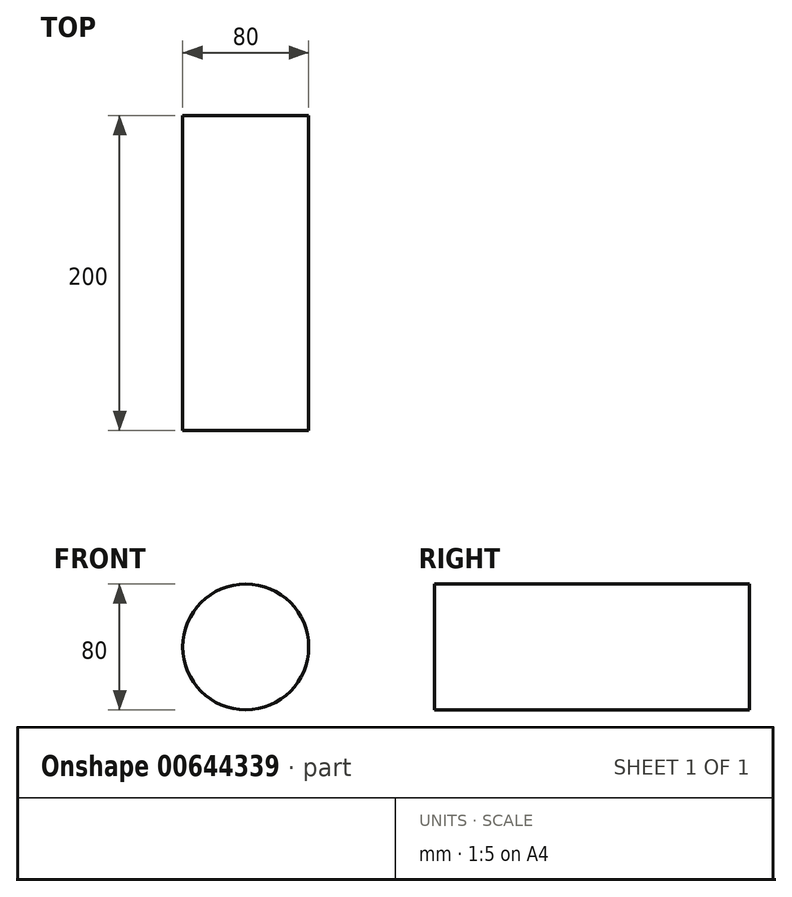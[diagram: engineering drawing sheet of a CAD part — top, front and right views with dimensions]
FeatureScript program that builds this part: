
annotation { "Feature Type Name" : "Feature", "Feature Type Description" : "" }
export const myFeature = defineFeature(function(context is Context, id is Id, definition is map)
    precondition{}
    {
        {
            var Q0;
            Q0=qCreatedBy(makeId("Front.planeOp"),FACE);
            var sketch = newSketch(context, id + "F0", { "sketchPlane" : qUnion([Q0])});
            skCircle(sketch, "E0", {"center": v(0, 0) * mm, "radius": 40 * mm});
            skSolve(sketch);
        }
        {
            var Q0;
            Q0 = qSketchRegion(id + "F0", true);
            extrude(context, id + "F1", {"entities" : qUnion([Q0]), "depth" : 200 * mm, "offsetDistance" : 25 * mm});
        }
        {
            var Q0;
            Q0=makeQuery(id+"F1.opExtrude","CAP_FACE",FACE,{"disambiguationData":[OSD([sQuery(id+"F0.wireOp",EDGE,"E0")])],"isStart":false});
            var sketch = newSketch(context, id + "F2", { "sketchPlane" : qUnion([Q0])});
            skCircle(sketch, "E1", {"center": v(0, 0) * mm, "radius": 27.5 * mm});
            skSolve(sketch);
        }
        {
            var Q0;
            Q0=makeQuery(id+"F2.imprint","IMPRINT",FACE,{"disambiguationData":[TD([[makeQuery(id+"F2.imprint","IMPRINT",EDGE,{"derivedFrom":sQuery(id+"F2.wireOp",EDGE,"E1")}),-1.0]])]});
            var Q1;
            Q1=makeQuery(id+"F2.imprint","IMPRINT",FACE,{"disambiguationData":[TD([[makeQuery(id+"F2.imprint","IMPRINT",EDGE,{"derivedFrom":sQuery(id+"F2.wireOp",EDGE,"E1")}),1.0]])]});
            var Q2;
            Q2 = qSketchRegion(id + "F4", true);
            extrude(context, id + "F3", {"entities" : qUnion([Q0, Q1, Q2]), "operationType" : NewBodyOperationType.ADD, "oppositeDirection" : true, "depth" : 200 * mm, "offsetDistance" : 25 * mm});
        }
    });
